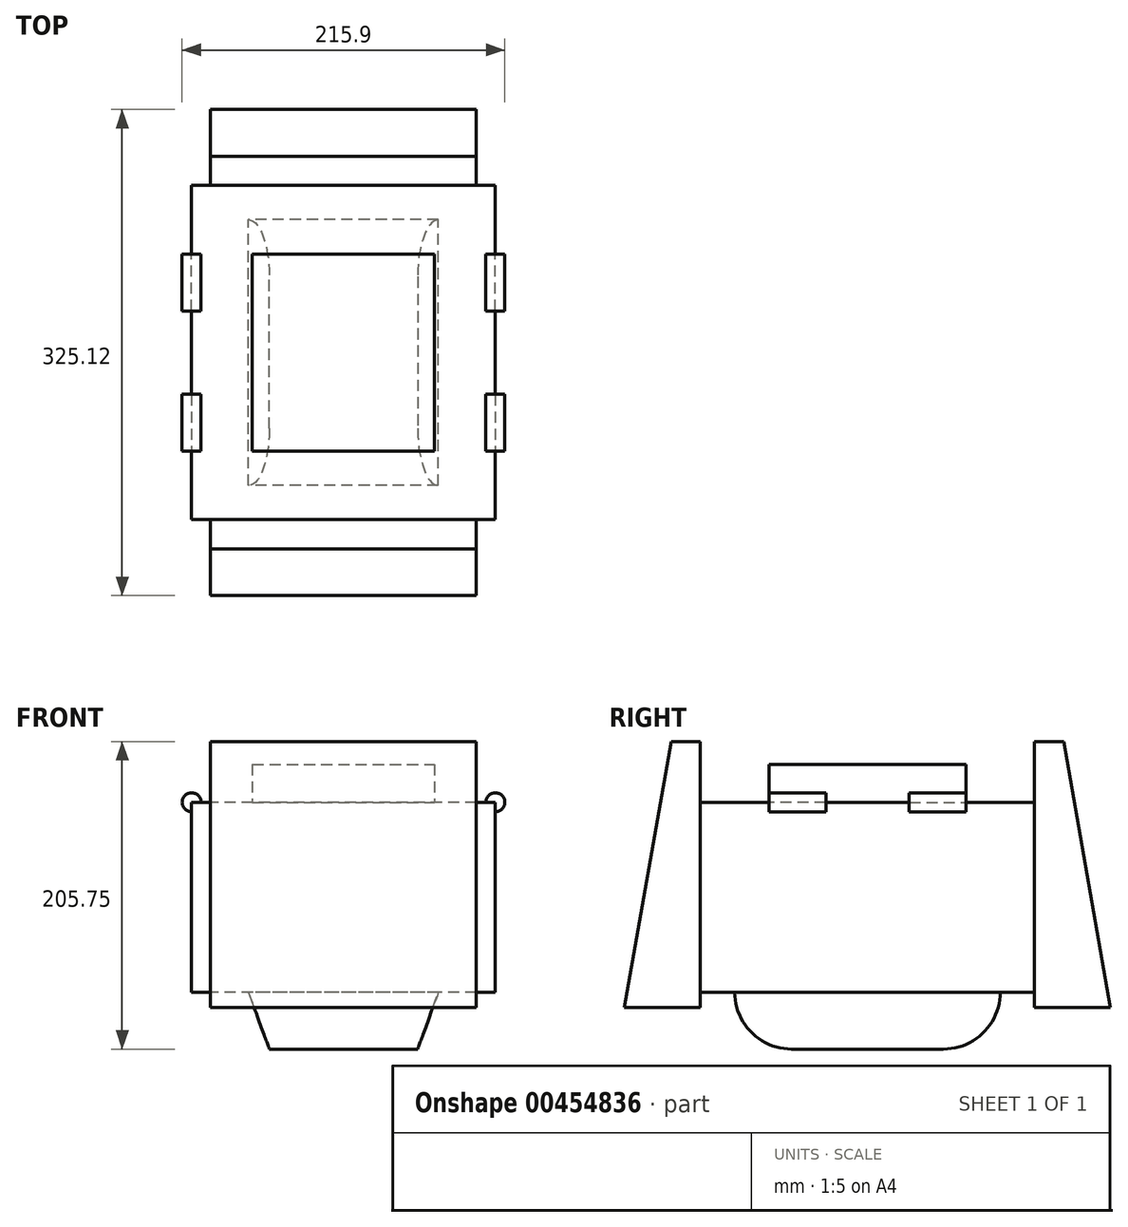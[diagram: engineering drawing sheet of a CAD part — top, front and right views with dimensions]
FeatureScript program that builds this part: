
annotation { "Feature Type Name" : "Feature", "Feature Type Description" : "" }
export const myFeature = defineFeature(function(context is Context, id is Id, definition is map)
    precondition{}
    {
        {
            var Q0;
            Q0=qCreatedBy(makeId("Front.planeOp"),FACE);
            var sketch = newSketch(context, id + "F0", { "sketchPlane" : qUnion([Q0])});
            skLineSegment(sketch, "E0.bottom", {"start": v(-60.96, 12.7) * mm, "end": v(60.96, 12.7) * mm});
            skLineSegment(sketch, "E0.top", {"start": v(-60.96, -12.7) * mm, "end": v(60.96, -12.7) * mm});
            skLineSegment(sketch, "E0.left", {"start": v(-60.96, 12.7) * mm, "end": v(-60.96, -12.7) * mm});
            skLineSegment(sketch, "E0.right", {"start": v(60.96, 12.7) * mm, "end": v(60.96, -12.7) * mm});
            skPoint(sketch, "E0.middle", {"position": v(0, 0) * mm});
            skSolve(sketch);
        }
        {
            var Q0;
            Q0 = qSketchRegion(id + "F0", true);
            extrude(context, id + "F1", {"entities" : qUnion([Q0]), "endBound" : BoundingType.SYMMETRIC, "depth" : 132 * mm, "offsetDistance" : 25.4 * mm});
        }
        {
            var Q0;
            Q0=makeQuery(id+"F1.opExtrude","SWEPT_FACE",FACE,{"disambiguationData":[OSD([sQuery(id+"F0.wireOp",EDGE,"E0.top")])]});
            var sketch = newSketch(context, id + "F2", { "sketchPlane" : qUnion([Q0])});
            skLineSegment(sketch, "E1.bottom", {"start": v(101.6, 111.76) * mm, "end": v(-101.6, 111.76) * mm});
            skLineSegment(sketch, "E1.top", {"start": v(101.6, -111.76) * mm, "end": v(-101.6, -111.76) * mm});
            skLineSegment(sketch, "E1.left", {"start": v(101.6, 111.76) * mm, "end": v(101.6, -111.76) * mm});
            skLineSegment(sketch, "E1.right", {"start": v(-101.6, 111.76) * mm, "end": v(-101.6, -111.76) * mm});
            skPoint(sketch, "E1.middle", {"position": v(0, 0) * mm});
            skSolve(sketch);
        }
        {
            var Q0;
            Q0 = qSketchRegion(id + "F2", true);
            extrude(context, id + "F3", {"entities" : qUnion([Q0]), "operationType" : NewBodyOperationType.ADD, "depth" : 25.4 * mm, "offsetDistance" : 25.4 * mm});
        }
        {
            var Q0;
            {var subQ0=sQuery(id+"F0.wireOp",EDGE,"E0.top");Q0=makeQuery(id+"F2.imprint","IMPRINT",FACE,{"disambiguationData":[TD([[makeQuery(id+"F2.imprint","IMPRINT",EDGE,{"derivedFrom":makeQuery(id+"F1.opExtrude","CAP_EDGE",EDGE,{"disambiguationData":[OSD([subQ0])],"isStart":true})}),1.0]])]});}
            var Q1;
            Q1=makeQuery(id+"F2.imprint","IMPRINT",FACE,{"disambiguationData":[TD([[makeQuery(id+"F2.imprint","IMPRINT",EDGE,{"derivedFrom":sQuery(id+"F2.wireOp",EDGE,"E1.bottom")}),1.0]])]});
            extrude(context, id + "F4", {"entities" : qUnion([Q0, Q1]), "operationType" : NewBodyOperationType.ADD, "depth" : 127 * mm, "offsetDistance" : 25.4 * mm});
        }
        {
            var Q0;
            Q0=makeQuery(id+"F4.opExtrude","CAP_FACE",FACE,{"disambiguationData":[OSD([sQuery(id+"F2.wireOp",EDGE,"E1.bottom"),sQuery(id+"F2.wireOp",EDGE,"E1.top"),sQuery(id+"F2.wireOp",EDGE,"E1.left"),sQuery(id+"F2.wireOp",EDGE,"E1.right")])],"isStart":false});
            var sketch = newSketch(context, id + "F5", { "sketchPlane" : qUnion([Q0])});
            skLineSegment(sketch, "E2.bottom", {"start": v(63.5, 88.9) * mm, "end": v(-63.5, 88.9) * mm});
            skLineSegment(sketch, "E2.top", {"start": v(63.5, -88.9) * mm, "end": v(-63.5, -88.9) * mm});
            skLineSegment(sketch, "E2.left", {"start": v(63.5, 88.9) * mm, "end": v(63.5, -88.9) * mm});
            skLineSegment(sketch, "E2.right", {"start": v(-63.5, 88.9) * mm, "end": v(-63.5, -88.9) * mm});
            skPoint(sketch, "E2.middle", {"position": v(0, 0) * mm});
            skSolve(sketch);
        }
        {
            var Q0;
            Q0 = qSketchRegion(id + "F5", true);
            extrude(context, id + "F6", {"entities" : qUnion([Q0]), "operationType" : NewBodyOperationType.ADD, "depth" : 38.1 * mm, "offsetDistance" : 25.4 * mm});
        }
        {
            var Q0;
            Q0=makeQuery(id+"F6.opExtrude","CAP_EDGE",EDGE,{"disambiguationData":[OSD([sQuery(id+"F5.wireOp",EDGE,"E2.bottom")])],"isStart":false});
            var Q1;
            Q1=makeQuery(id+"F6.opExtrude","CAP_EDGE",EDGE,{"disambiguationData":[OSD([sQuery(id+"F5.wireOp",EDGE,"E2.top")])],"isStart":false});
            fillet(context, id + "F7", {"entities" : qUnion([Q0, Q1]), "radius" : 38.1 * mm, "tangentPropagation" : true, "allowEdgeOverflow" : false});
        }
        {
            var Q0;
            Q0=makeQuery(id+"F6.opExtrude","CAP_EDGE",EDGE,{"disambiguationData":[OSD([sQuery(id+"F5.wireOp",EDGE,"E2.left")])],"isStart":false});
            var Q1;
            Q1=makeQuery(id+"F6.opExtrude","CAP_EDGE",EDGE,{"disambiguationData":[OSD([sQuery(id+"F5.wireOp",EDGE,"E2.right")])],"isStart":false});
            chamfer(context, id + "F8", {"entities" : qUnion([Q0, Q1]), "chamferType" : ChamferType.OFFSET_ANGLE, "width" : 38.1 * mm, "oppositeDirection" : false, "angle" : 20 * degree, "tangentPropagation" : true});
        }
        {
            var Q0;
            {var subQ0=sQuery(id+"F2.wireOp",EDGE,"E1.bottom");Q0=makeQuery(id+"F4.boolean.opBoolean","MERGE",FACE,{"derivedFrom":[makeQuery(id+"F3.opExtrude","SWEPT_FACE",FACE,{"disambiguationData":[OSD([subQ0])]}),makeQuery(id+"F4.opExtrude","SWEPT_FACE",FACE,{"disambiguationData":[OSD([subQ0])]})]});}
            var sketch = newSketch(context, id + "F9", { "sketchPlane" : qUnion([Q0])});
            skLineSegment(sketch, "E3.bottom", {"start": v(88.9, 27.94) * mm, "end": v(-88.9, 27.94) * mm});
            skLineSegment(sketch, "E3.top", {"start": v(88.9, -149.86) * mm, "end": v(-88.9, -149.86) * mm});
            skLineSegment(sketch, "E3.left", {"start": v(88.9, 27.94) * mm, "end": v(88.9, -149.86) * mm});
            skLineSegment(sketch, "E3.right", {"start": v(-88.9, 27.94) * mm, "end": v(-88.9, -149.86) * mm});
            skPoint(sketch, "E3.middle", {"position": v(0, -88.9) * mm});
            skSolve(sketch);
        }
        {
            var Q0;
            Q0 = qSketchRegion(id + "F9", true);
            extrude(context, id + "F10", {"entities" : qUnion([Q0]), "operationType" : NewBodyOperationType.ADD, "depth" : 50.8 * mm, "offsetDistance" : 25.4 * mm});
        }
        {
            var Q0;
            Q0=makeQuery(id+"F10.opExtrude","CAP_EDGE",EDGE,{"disambiguationData":[OSD([sQuery(id+"F9.wireOp",EDGE,"E3.bottom")])],"isStart":false});
            chamfer(context, id + "F11", {"entities" : qUnion([Q0]), "chamferType" : ChamferType.OFFSET_ANGLE, "width" : 177.8 * mm, "oppositeDirection" : false, "angle" : 10 * degree, "tangentPropagation" : true});
        }
        {
            var Q0;
            {var subQ0=sQuery(id+"F2.wireOp",EDGE,"E1.top");Q0=makeQuery(id+"F4.boolean.opBoolean","MERGE",FACE,{"derivedFrom":[makeQuery(id+"F3.opExtrude","SWEPT_FACE",FACE,{"disambiguationData":[OSD([subQ0])]}),makeQuery(id+"F4.opExtrude","SWEPT_FACE",FACE,{"disambiguationData":[OSD([subQ0])]})]});}
            var sketch = newSketch(context, id + "F12", { "sketchPlane" : qUnion([Q0])});
            skLineSegment(sketch, "E4.bottom", {"start": v(-88.9, 27.95) * mm, "end": v(88.9, 27.95) * mm});
            skLineSegment(sketch, "E4.top", {"start": v(-88.9, -149.85) * mm, "end": v(88.9, -149.85) * mm});
            skLineSegment(sketch, "E4.left", {"start": v(-88.9, 27.95) * mm, "end": v(-88.9, -149.85) * mm});
            skLineSegment(sketch, "E4.right", {"start": v(88.9, 27.95) * mm, "end": v(88.9, -149.85) * mm});
            skSolve(sketch);
        }
        {
            var Q0;
            Q0 = qSketchRegion(id + "F12", true);
            extrude(context, id + "F13", {"entities" : qUnion([Q0]), "operationType" : NewBodyOperationType.ADD, "depth" : 50.8 * mm, "offsetDistance" : 25.4 * mm});
        }
        {
            var Q0;
            Q0=makeQuery(id+"F13.opExtrude","CAP_EDGE",EDGE,{"disambiguationData":[OSD([sQuery(id+"F12.wireOp",EDGE,"E4.bottom")])],"isStart":false});
            chamfer(context, id + "F14", {"entities" : qUnion([Q0]), "chamferType" : ChamferType.OFFSET_ANGLE, "width" : 177.8 * mm, "oppositeDirection" : true, "angle" : 10 * degree, "tangentPropagation" : true});
        }
        {
            var Q0;
            Q0=makeQuery(id+"F1.opExtrude","CAP_FACE",FACE,{"disambiguationData":[OSD([sQuery(id+"F0.wireOp",EDGE,"E0.bottom"),sQuery(id+"F0.wireOp",EDGE,"E0.top"),sQuery(id+"F0.wireOp",EDGE,"E0.left"),sQuery(id+"F0.wireOp",EDGE,"E0.right")])],"isStart":true});
            var sketch = newSketch(context, id + "F15", { "sketchPlane" : qUnion([Q0])});
            skCircle(sketch, "E5", {"center": v(101.6, -12.7) * mm, "radius": 6.35 * mm});
            skSolve(sketch);
        }
        {
            var Q0;
            Q0 = qSketchRegion(id + "F15", true);
            extrude(context, id + "F16", {"entities" : qUnion([Q0]), "operationType" : NewBodyOperationType.ADD, "depth" : -38.1 * mm, "offsetDistance" : 25.4 * mm});
        }
        {
            var Q0;
            Q0=makeQuery(id+"F1.opExtrude","CAP_FACE",FACE,{"disambiguationData":[OSD([sQuery(id+"F0.wireOp",EDGE,"E0.bottom"),sQuery(id+"F0.wireOp",EDGE,"E0.top"),sQuery(id+"F0.wireOp",EDGE,"E0.left"),sQuery(id+"F0.wireOp",EDGE,"E0.right")])],"isStart":false});
            var sketch = newSketch(context, id + "F17", { "sketchPlane" : qUnion([Q0])});
            skCircle(sketch, "E6", {"center": v(-101.6, -12.7) * mm, "radius": 6.35 * mm});
            skSolve(sketch);
        }
        {
            var Q0;
            Q0 = qSketchRegion(id + "F17", true);
            extrude(context, id + "F18", {"entities" : qUnion([Q0]), "operationType" : NewBodyOperationType.ADD, "depth" : -38.1 * mm, "offsetDistance" : 25.4 * mm});
        }
        {
            var Q0;
            Q0=makeQuery(id+"F1.opExtrude","CAP_FACE",FACE,{"disambiguationData":[OSD([sQuery(id+"F0.wireOp",EDGE,"E0.bottom"),sQuery(id+"F0.wireOp",EDGE,"E0.top"),sQuery(id+"F0.wireOp",EDGE,"E0.left"),sQuery(id+"F0.wireOp",EDGE,"E0.right")])],"isStart":false});
            var sketch = newSketch(context, id + "F19", { "sketchPlane" : qUnion([Q0])});
            skCircle(sketch, "E7", {"center": v(101.6, -12.7) * mm, "radius": 6.35 * mm});
            skSolve(sketch);
        }
        {
            var Q0;
            Q0 = qSketchRegion(id + "F19", true);
            extrude(context, id + "F20", {"entities" : qUnion([Q0]), "operationType" : NewBodyOperationType.ADD, "depth" : -38.1 * mm, "offsetDistance" : 25.4 * mm});
        }
        {
            var Q0;
            Q0=makeQuery(id+"F1.opExtrude","CAP_FACE",FACE,{"disambiguationData":[OSD([sQuery(id+"F0.wireOp",EDGE,"E0.bottom"),sQuery(id+"F0.wireOp",EDGE,"E0.top"),sQuery(id+"F0.wireOp",EDGE,"E0.left"),sQuery(id+"F0.wireOp",EDGE,"E0.right")])],"isStart":true});
            var sketch = newSketch(context, id + "F21", { "sketchPlane" : qUnion([Q0])});
            skCircle(sketch, "E8", {"center": v(-101.6, -12.7) * mm, "radius": 6.35 * mm});
            skSolve(sketch);
        }
        {
            var Q0;
            Q0 = qSketchRegion(id + "F21", true);
            extrude(context, id + "F22", {"entities" : qUnion([Q0]), "operationType" : NewBodyOperationType.ADD, "depth" : -38.1 * mm, "offsetDistance" : 25.4 * mm});
        }
    });
